# Revit family: RRGCLM
name_source: partatom
category: Generic Models
revit_build: Autodesk Revit 2018 (Build: 20190510_1515(x64)
units: mm (PartAtom-declared; Revit-internal decimal feet)

## family parameters
Always vertical = No
Can host rebar = No
Cut with Voids When Loaded = No
Part Type = Normal
Room Calculation Point = No
Round Connector Dimension = Use Diameter
Shared = Yes
Work Plane-Based = Yes

## types (6) — shared parameters
Default Elevation = 48 "
Description = Industrial 2 Piece Clamp for Conduit
Screw Radius = 0.075 "

## per-type parameters (varying)
| type | Clamp Height | Coupler Height | Height | Inner Radius | Outer Radius | Pipe Radius | Pipe Size | Screw Offset | Slot Offset | Tab Offset | Width |
| RRGCLM.SRC100 | 1.125 " | 0.337 " | 2 " | 0.725 " | 0.875 " | 0.5 " | 1" | 0.25 " | 0.975 " | 0.775 " | 2.75 " |
| RRGCLM.SRC50 | 0.75 " | 0.399 " | 1.188 " | 0.288 " | 0.438 " | 0.25 " | 1" | 0.312 " | 0.538 " | 0.318 " | 2.125 " |
| RRGCLM.SRC200 | 1.625 " | 0.274 " | 3.063 " | 1.288 " | 1.438 " | 1 " | 2" | 0.266 " | 1.538 " | 1.338 " | 3.938 " |
| RRGCLM.SRC75 | 0.875 " | 0.274 " | 1.563 " | 0.538 " | 0.688 " | 0.375 " | 1" | 0.281 " | 0.788 " | 0.588 " | 2.5 " |
| RRGCLM.SRC125 | 1.313 " | 0.338 " | 2.375 " | 0.912 " | 1.062 " | 0.625 " | 1" | 0.266 " | 1.162 " | 0.962 " | 3.188 " |
| RRGCLM.SRC150 | 1.438 " | 0.338 " | 2.625 " | 1.037 " | 1.187 " | 0.75 " | 2" | 0.25 " | 1.287 " | 1.087 " | 3.375 " |

note: column(s) folded — value = type name in every type: Catalog Number

## geometry (parser evidence)
native form markers: Sweep x10
no freeform markers — native parametric forms only
